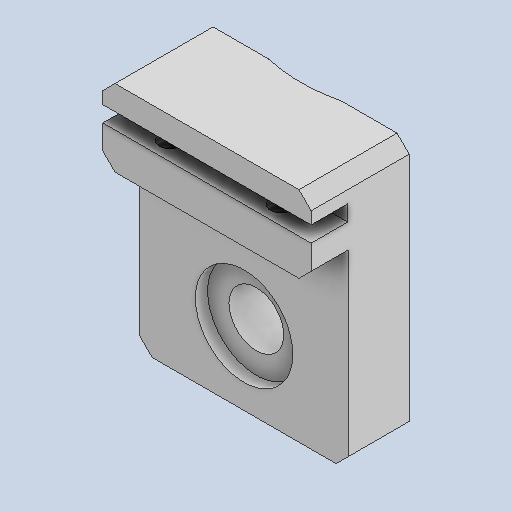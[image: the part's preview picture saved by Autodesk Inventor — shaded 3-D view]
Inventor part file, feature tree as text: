
AUTODESK INVENTOR PART (.ipt)
format: ipt  version: 2024.2 (Build 282272000, 272)  size: 228,352 bytes
history: native  units: in
note: dims shown in document units (in); Inventor stores cm internally (conversion verified against a paired STEP export)
features: extrude x6, hole x3, chamfer x1
ambient origin geometry x8: Origin, YZ Plane, XZ Plane, XY Plane, X Axis, Y Axis, Z Axis, Center Point
bodies: Solid1 (feature_tree)
feature tree (10):
  extrude  "Extrusion1"  Depth=0.4134in
  hole  "Hole1"  [1 undecoded]
  extrude  "Extrusion2"  Depth=0.1969in TaperAngle=0.0deg
  extrude  "Extrusion6"  Depth=0.4134in
  extrude  "Extrusion5"  Depth=0.248in
  hole  "Hole2"  [1 undecoded]
  hole  "Hole3"  [1 undecoded]
  extrude  "Extrusion4"  Depth=0.2362in
  chamfer  "Chamfer1"  Distance=0.6732in
  extrude  "Extrusion7"  Depth=0.6732in
note: 3 required parameter values undecoded (feature->parameter linkage not recoverable at this tier; creation-order binding heuristic only, values carry confidence <= 0.55)
